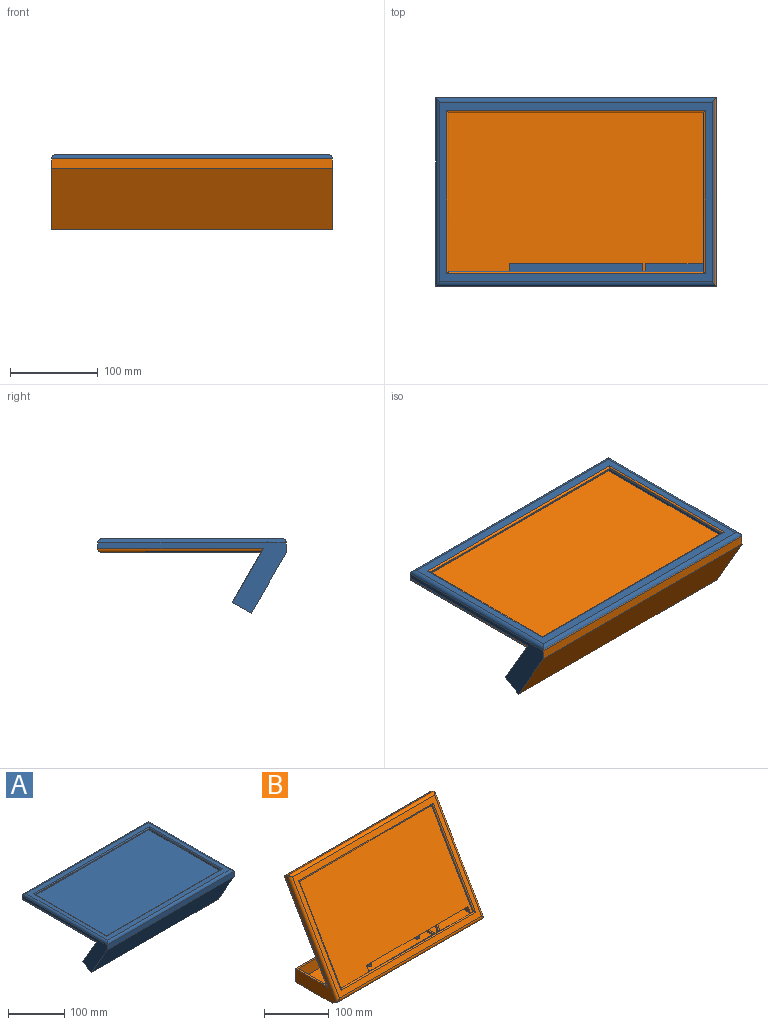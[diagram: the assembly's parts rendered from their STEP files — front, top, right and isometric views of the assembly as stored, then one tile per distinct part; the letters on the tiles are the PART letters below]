
ASSEMBLY  parts=2 mates=1
PART A: 33 faces, bbox 320x215x85.3 mm
  f0: plane 300x196.34mm, normal (0,0,1), area 58901.9mm2, adj f11,f13,f14,f30
  f1: plane 215x80.28mm, normal (1,0,0), area 3246.7mm2, adj f2,f4,f16,f17,f18,f19,f27
  f2: plane 320x6mm, normal (0,1,0), area 1920mm2, adj f1,f3,f21,f28
  f3: plane 215x81.78mm, normal (-1,0,0), area 3249.3mm2, adj f2,f4,f16,f17,f18,f22,f29,f31
  f4: plane 320x11mm, normal (0,-1,0), area 3520mm2, adj f1,f3,f17,f20
  f5: plane 310x205mm, normal (0,0,1), area 9160mm2, adj f19,f20,f21,f22,f23,f24,f25,f26
  f6: plane 310x181.13mm, normal (0,0,-1), area 56151.1mm2, adj f16,f27,f28,f29
  f7: plane 181x1mm, normal (1,0,0), area 181mm2, adj f8,f10,f15,f23
  f8: plane 290x1mm, normal (0,1,0), area 290mm2, adj f7,f9,f15,f25
  f9: plane 181x1mm, normal (-1,0,0), area 181mm2, adj f8,f10,f15,f26
  f10: plane 290x1mm, normal (0,-1,0), area 290mm2, adj f7,f9,f15,f24
  f11: plane 196.34x8mm, normal (1,0,0), area 1560.5mm2, adj f0,f12,f14,f15,f30
  f12: plane 300x7.23mm, normal (0,1,0), area 2167.9mm2, adj f11,f13,f15,f30
  f13: plane 196.34x8mm, normal (-1,0,0), area 1560.5mm2, adj f0,f12,f14,f15,f30
  f14: plane 300x8mm, normal (0,-1,0), area 2400mm2, adj f0,f11,f13,f15
  f15: plane 300x195mm, normal (0,0,-1), area 6010mm2, adj f7,f8,f9,f10,f11,f12,f13,f14
  f16: plane 320x61.78mm, normal (0,0.87,0.5), area 20993.6mm2, adj f1,f3,f6,f18,f27,f29
  f17: plane 320x69.28mm, normal (0,-0.87,-0.5), area 25600mm2, adj f1,f3,f4,f18
  f18: plane 320x21.65mm, normal (0,0.5,-0.87), area 8000mm2, adj f1,f3,f16,f17
  f19: cylinder r=5mm len=215mm, axis (0,-1,0), area 1660.1mm2, adj f1,f5,f20,f21
  f20: cylinder r=5mm len=320mm, axis (-1,0,0), area 2484.7mm2, adj f4,f5,f19,f22
  f21: cylinder r=5mm len=320mm, axis (1,0,0), area 2484.7mm2, adj f2,f5,f19,f22
  f22: cylinder r=5mm len=215mm, axis (0,1,0), area 1657.4mm2, adj f3,f5,f20,f21,f31,f32
  f23: cylinder r=2mm len=185mm, axis (0,1,0), area 573.2mm2, adj f5,f7,f24,f25
  f24: cylinder r=2mm len=294mm, axis (1,0,0), area 915.6mm2, adj f5,f10,f23,f26
  f25: cylinder r=2mm len=294mm, axis (-1,0,0), area 915.6mm2, adj f5,f8,f23,f26
  f26: cylinder r=2mm len=185mm, axis (0,-1,0), area 573.2mm2, adj f5,f9,f24,f25
  f27: cylinder r=5mm len=189.02mm, axis (0,1,0), area 1455.8mm2, adj f1,f6,f16,f28
  f28: cylinder r=5mm len=320mm, axis (-1,0,0), area 2484.7mm2, adj f2,f6,f27,f29
  f29: cylinder r=5mm len=189.02mm, axis (0,-1,0), area 1455.8mm2, adj f3,f6,f16,f28
  f30: plane 300x1.34mm, normal (0,0.5,-0.87), area 464.1mm2, adj f0,f11,f12,f13
  f31: plane 1.51x0.88mm, normal (0,0.87,0.5), area 0.1mm2, adj f3,f22,f32
  f32: plane 2.6x1.5mm, normal (0,-0.5,0.87), area 0.2mm2, adj f3,f22,f31
PART B: 89 faces, bbox 320x121.4x194.2 mm
  f0: plane 155.2x33.66mm, normal (0,0,1), area 2279.8mm2, adj f2,f3,f7,f10,f71,f86,f88
  f1: plane 66x0.38mm, normal (0,0,1), area 25.4mm2, adj f2,f5,f71,f85
  f2: plane 300x6.48mm, normal (0,1,0), area 1541.7mm2, adj f0,f1,f3,f5,f10,f45,f46,f47
  f3: plane 78x23mm, normal (-1,0,0), area 1323.5mm2, adj f0,f2,f4,f6,f7,f11,f12,f58
  f4: plane 152.4x5.77mm, normal (0,0,-1), area 879.9mm2, adj f3,f10,f52,f58
  f5: plane 19.93x11.89mm, normal (-1,0,0), area 57.4mm2, adj f1,f2,f29,f58,f85
  f6: plane 320x71.34mm, normal (0,0,1), area 1488.6mm2, adj f3,f8,f10,f11,f32,f34,f52,f55
  f7: plane 152.4x3.07mm, normal (0,1,0), area 467.3mm2, adj f0,f3,f10,f12
  f8: plane 320x25mm, normal (0,1,0), area 8000mm2, adj f6,f9,f55,f57
  f9: plane 320x80mm, normal (0,0,-1), area 25600mm2, adj f8,f54,f55,f57
  f10: plane 78x23mm, normal (1,0,0), area 1684.6mm2, adj f0,f2,f4,f6,f7,f11,f12,f58
  f11: plane 152.4x23mm, normal (0,-1,0), area 3505.2mm2, adj f3,f6,f10,f12
  f12: plane 152.4x63.5mm, normal (0,0,1), area 9498.3mm2, adj f3,f7,f10,f11,f13,f16,f19,f22
  f13: cylinder r=3.78mm len=7.55mm, axis (0,0,-1), area 71.2mm2, adj f12,f14
  f14: plane 7.55x7.55mm, normal (0,0,1), area 38.8mm2, adj f13,f15
  f15: cylinder r=1.38mm len=3mm, axis (0,0,1), area 25.9mm2, adj f14,f28
  f16: cylinder r=3.78mm len=7.55mm, axis (0,0,-1), area 71.2mm2, adj f12,f17
  f17: plane 7.55x7.55mm, normal (0,0,1), area 38.8mm2, adj f16,f18
  f18: cylinder r=1.38mm len=3mm, axis (0,0,1), area 25.9mm2, adj f17,f27
  f19: cylinder r=3.78mm len=7.55mm, axis (0,0,-1), area 71.2mm2, adj f12,f20
  f20: plane 7.55x7.55mm, normal (0,0,1), area 38.8mm2, adj f19,f21
  f21: cylinder r=1.38mm len=3mm, axis (0,0,1), area 25.9mm2, adj f20,f26
  f22: cylinder r=3.78mm len=7.55mm, axis (0,0,-1), area 71.2mm2, adj f12,f23
  f23: plane 7.55x7.55mm, normal (0,0,1), area 38.8mm2, adj f22,f24
  f24: cylinder r=1.38mm len=3mm, axis (0,0,1), area 25.9mm2, adj f23,f25
  f25: plane 2.75x2.75mm, normal (0,0,1), area 5.9mm2, adj f24
  f26: plane 2.75x2.75mm, normal (0,0,1), area 5.9mm2, adj f21
  f27: plane 2.75x2.75mm, normal (0,0,1), area 5.9mm2, adj f18
  f28: plane 2.75x2.75mm, normal (0,0,1), area 5.9mm2, adj f15
  f29: plane 78.2x5.77mm, normal (0,0,-1), area 415.9mm2, adj f5,f34,f52,f58,f61,f71,f75,f81
  f30: plane 3x0.23mm, normal (0,-1,0), area 0.2mm2, adj f31,f39,f55
  f31: plane 1.74x0.24mm, normal (0,0,1), area 0.1mm2, adj f30,f39,f55
  f32: cylinder r=5mm len=166.2mm, axis (0,-0.5,-0.87), area 1455.8mm2, adj f6,f33,f52,f55,f67
  f33: cylinder r=5mm len=320mm, axis (-1,0,0), area 2484.7mm2, adj f32,f34,f52,f56
  f34: cylinder r=5mm len=166.2mm, axis (0,0.5,0.87), area 1455.8mm2, adj f6,f29,f33,f52,f57
  f35: cylinder r=2mm len=161.21mm, axis (0,-0.5,-0.87), area 573.2mm2, adj f36,f37,f49,f53
  f36: cylinder r=2mm len=294mm, axis (-1,0,0), area 915.6mm2, adj f35,f38,f50,f53
  f37: cylinder r=2mm len=294mm, axis (1,0,0), area 915.6mm2, adj f35,f38,f48,f53
  f38: cylinder r=2mm len=161.21mm, axis (0,0.5,0.87), area 573.2mm2, adj f36,f37,f51,f53
  f39: cylinder r=5mm len=188.7mm, axis (0,0.5,0.87), area 1657.4mm2, adj f30,f31,f40,f41,f53,f55
  f40: cylinder r=5mm len=320mm, axis (1,0,0), area 2484.7mm2, adj f39,f42,f53,f56
  f41: cylinder r=5mm len=320mm, axis (-1,0,0), area 2484.7mm2, adj f39,f42,f53,f54
  f42: cylinder r=5mm len=188.7mm, axis (0,-0.5,-0.87), area 1660.1mm2, adj f40,f41,f53,f57
  f43: plane 300x168.88mm, normal (0,0.87,-0.5), area 6010mm2, adj f44,f45,f46,f47,f48,f49,f50,f51
  f44: plane 300x6.93mm, normal (0,-0.5,-0.87), area 2400mm2, adj f43,f45,f47,f58
  f45: plane 174.04x104.43mm, normal (-1,0,0), area 1560.5mm2, adj f2,f43,f44,f46,f58
  f46: plane 300x6.26mm, normal (0,0.5,0.87), area 2167.9mm2, adj f2,f43,f45,f47
  f47: plane 174.04x104.43mm, normal (1,0,0), area 1560.5mm2, adj f2,f43,f44,f46,f58
  f48: plane 290x0.87mm, normal (0,-0.5,-0.87), area 290mm2, adj f37,f43,f49,f51
  f49: plane 157.25x91.37mm, normal (-1,0,0), area 181mm2, adj f35,f43,f48,f50
  f50: plane 290x0.87mm, normal (0,0.5,0.87), area 290mm2, adj f36,f43,f49,f51
  f51: plane 157.25x91.37mm, normal (1,0,0), area 181mm2, adj f38,f43,f48,f50
  f52: plane 310x156.87mm, normal (0,0.87,-0.5), area 56151.1mm2, adj f4,f6,f29,f32,f33,f34,f67
  f53: plane 310x177.54mm, normal (0,-0.87,0.5), area 9160mm2, adj f35,f36,f37,f38,f39,f40,f41,f42
  f54: plane 320x9.53mm, normal (0,-0.5,-0.87), area 3520mm2, adj f9,f41,f55,f57
  f55: plane 191.7x112.7mm, normal (-1,0,0), area 3249.3mm2, adj f6,f8,f9,f30,f31,f32,f39,f54
  f56: plane 320x5.2mm, normal (0,0.5,0.87), area 1920mm2, adj f33,f40,f55,f57
  f57: plane 191.7x112.7mm, normal (1,0,0), area 3246.7mm2, adj f6,f8,f9,f34,f42,f54,f56
  f58: plane 300x170.04mm, normal (0,-0.87,0.5), area 55119.1mm2, adj f2,f3,f4,f5,f10,f29,f44,f45
  f59: plane 310x177.54mm, normal (0,0.87,-0.5), area 2246.6mm2, adj f60,f61,f63,f76,f77,f78,f79,f80
  f60: plane 305.6x9.01mm, normal (0,0.5,0.87), area 3178.2mm2, adj f59,f61,f63,f81
  f61: plane 183.04x109.31mm, normal (1,0,0), area 2115.6mm2, adj f29,f59,f60,f62,f72,f80,f81,f85
  f62: plane 314.4x8.88mm, normal (0,0.5,0.87), area 2183.7mm2, adj f61,f63,f64,f65,f69,f70,f71,f72
  f63: plane 183.04x109.31mm, normal (-1,0,0), area 2115.6mm2, adj f59,f60,f62,f65,f67,f72,f80,f81
  f64: plane 78.2x76.45mm, normal (0,0,1), area 5978.4mm2, adj f62,f68,f71,f84
  f65: plane 73.8x21.48mm, normal (0,0.87,-0.5), area 1830mm2, adj f62,f63,f67,f70
  f66: plane 78.2x22.2mm, normal (0,-1,0), area 1736mm2, adj f6,f69,f70,f82
  f67: plane 78.2x5.77mm, normal (0,0,-1), area 202.5mm2, adj f32,f52,f63,f65,f70,f73,f81,f82
  f68: plane 78.2x22.2mm, normal (0,-1,0), area 1736mm2, adj f6,f64,f71,f84
  f69: plane 78.2x76.45mm, normal (0,0,1), area 5978.4mm2, adj f62,f66,f70,f82
  f70: plane 77.71x22.2mm, normal (-1,0,0), area 1591.5mm2, adj f6,f62,f65,f66,f67,f69
  f71: plane 77.71x22.2mm, normal (1,0,0), area 1287.8mm2, adj f0,f1,f2,f6,f29,f58,f62,f64
  f72: plane 305.6x5.08mm, normal (0,-1,0), area 1552.7mm2, adj f61,f62,f63,f80
  f73: cylinder r=2.2mm len=162.37mm, axis (0,-0.5,-0.87), area 638mm2, adj f67,f74,f81,f82
  f74: cylinder r=2.2mm len=314.4mm, axis (-1,0,0), area 1081mm2, adj f73,f75,f81,f83
  f75: cylinder r=2.2mm len=162.37mm, axis (0,0.5,0.87), area 638mm2, adj f29,f74,f81,f84
  f76: cylinder r=2.2mm len=182.45mm, axis (0,0.5,0.87), area 718.1mm2, adj f59,f77,f78,f82
  f77: cylinder r=2.2mm len=314.4mm, axis (1,0,0), area 1081mm2, adj f59,f76,f79,f83
  f78: cylinder r=2.2mm len=314.4mm, axis (-1,0,0), area 1081mm2, adj f59,f62,f76,f79
  f79: cylinder r=2.2mm len=182.45mm, axis (0,-0.5,-0.87), area 718.1mm2, adj f59,f77,f78,f84
  f80: plane 305.6x5.03mm, normal (0,-0.5,-0.87), area 1775.5mm2, adj f59,f61,f63,f72
  f81: plane 310x158.27mm, normal (0,-0.87,0.5), area 1476.4mm2, adj f29,f60,f61,f63,f67,f73,f74,f75
  f82: plane 186.47x109.9mm, normal (1,0,0), area 2915mm2, adj f6,f62,f66,f67,f69,f73,f76,f83
  f83: plane 314.4x5.2mm, normal (0,-0.5,-0.87), area 1886.4mm2, adj f74,f77,f82,f84
  f84: plane 186.47x109.9mm, normal (-1,0,0), area 2915mm2, adj f6,f29,f62,f64,f68,f75,f79,f83
  f85: plane 73.8x21.48mm, normal (0,0.87,-0.5), area 310.9mm2, adj f1,f5,f29,f61,f62,f71
  f86: plane 14.44x2.8mm, normal (0,-1,0), area 40.4mm2, adj f0,f3,f71,f87
  f87: plane 25x2.8mm, normal (0,0,-1), area 70mm2, adj f3,f71,f86,f88
  f88: plane 14.44x2.8mm, normal (0,1,0), area 40.4mm2, adj f0,f3,f71,f87
PLACE A t=(-764.43,-109.21,116.69)mm
PLACE B rot(axis=(-1,0,0),60deg) t=(-769.87,-126.46,64.01)mm
MATE fastened A.f18 <-> B.f8  axis (0,0.5,-0.87) through (-765.52,-116.87,47.41)mm
